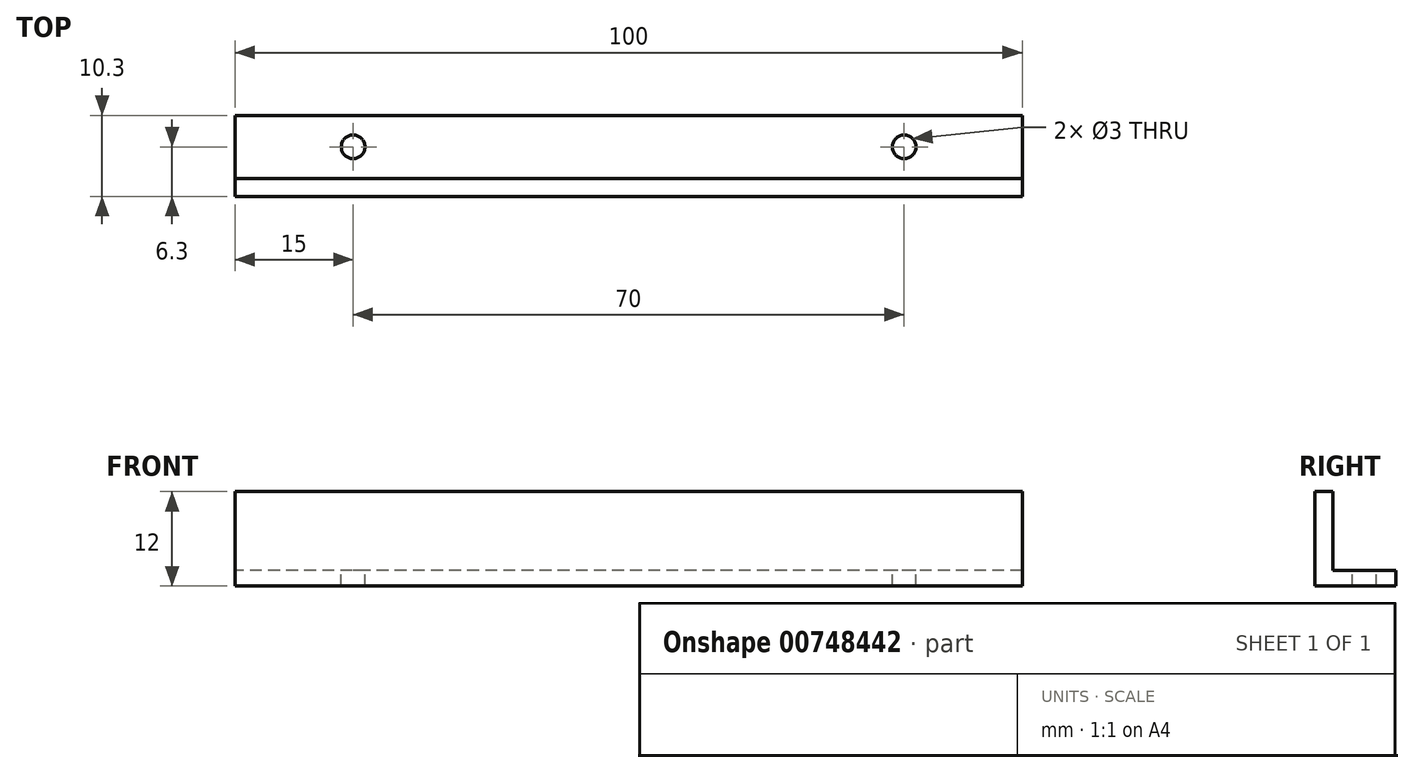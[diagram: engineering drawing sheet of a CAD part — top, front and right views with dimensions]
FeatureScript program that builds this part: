
annotation { "Feature Type Name" : "Feature", "Feature Type Description" : "" }
export const myFeature = defineFeature(function(context is Context, id is Id, definition is map)
    precondition{}
    {
        {
            var Q0;
            Q0=qCreatedBy(makeId("Right.planeOp"),FACE);
            var sketch = newSketch(context, id + "F0", { "sketchPlane" : qUnion([Q0])});
            skLineSegment(sketch, "E0", {"start": v(0, 0) * mm, "end": v(10.3, 0) * mm});
            skLineSegment(sketch, "E1", {"start": v(10.3, 0) * mm, "end": v(10.3, 2) * mm});
            skLineSegment(sketch, "E2", {"start": v(10.3, 2) * mm, "end": v(2.3, 2) * mm});
            skLineSegment(sketch, "E3", {"start": v(2.3, 2) * mm, "end": v(2.3, 12) * mm});
            skLineSegment(sketch, "E4", {"start": v(2.3, 12) * mm, "end": v(0, 12) * mm});
            skLineSegment(sketch, "E5", {"start": v(0, 12) * mm, "end": v(0, 0) * mm});
            skSolve(sketch);
        }
        {
            var Q0;
            Q0=makeQuery(id+"F0.imprint","IMPRINT",FACE,{"disambiguationData":[TD([[makeQuery(id+"F0.imprint","IMPRINT",EDGE,{"derivedFrom":sQuery(id+"F0.wireOp",EDGE,"E0")}),1.0]])]});
            extrude(context, id + "F1", {"entities" : qUnion([Q0]), "depth" : 100 * mm, "offsetDistance" : 25 * mm});
        }
        {
            var Q0;
            Q0=makeQuery(id+"F1.opExtrude","SWEPT_FACE",FACE,{"disambiguationData":[OSD([sQuery(id+"F0.wireOp",EDGE,"E2")])]});
            var sketch = newSketch(context, id + "F2", { "sketchPlane" : qUnion([Q0])});
            skLineSegment(sketch, "E6", {"start": v(100, 6.3) * mm, "end": v(85, 6.3) * mm, "construction": true});
            skLineSegment(sketch, "E7", {"start": v(85, 6.3) * mm, "end": v(15, 6.3) * mm, "construction": true});
            skLineSegment(sketch, "E8", {"start": v(15, 6.3) * mm, "end": v(0, 6.3) * mm, "construction": true});
            skCircle(sketch, "E9", {"center": v(85, 6.3) * mm, "radius": 1.5 * mm});
            skCircle(sketch, "E10", {"center": v(15, 6.3) * mm, "radius": 1.5 * mm});
            skSolve(sketch);
        }
        {
            var Q0;
            Q0=makeQuery(id+"F2.imprint","IMPRINT",FACE,{"disambiguationData":[TD([[makeQuery(id+"F2.imprint","IMPRINT",EDGE,{"derivedFrom":sQuery(id+"F2.wireOp",EDGE,"E9")}),1.0]])]});
            var Q1;
            Q1=makeQuery(id+"F2.imprint","IMPRINT",FACE,{"disambiguationData":[TD([[makeQuery(id+"F2.imprint","IMPRINT",EDGE,{"derivedFrom":sQuery(id+"F2.wireOp",EDGE,"E10")}),1.0]])]});
            extrude(context, id + "F3", {"entities" : qUnion([Q0, Q1]), "operationType" : NewBodyOperationType.REMOVE, "oppositeDirection" : true, "depth" : 25 * mm, "offsetDistance" : 25 * mm});
        }
    });
